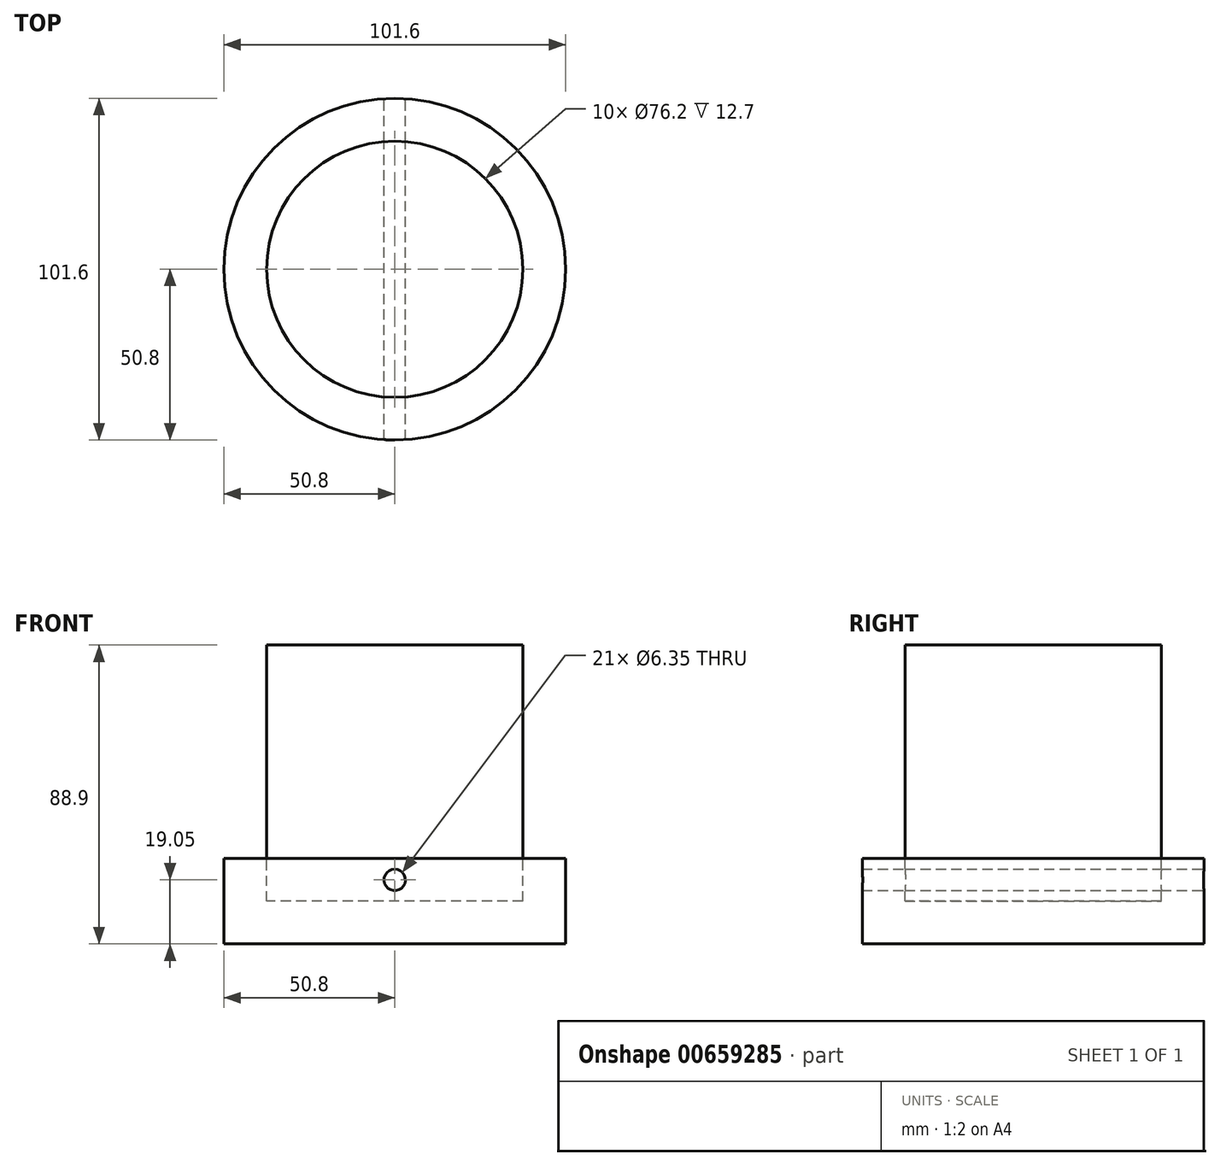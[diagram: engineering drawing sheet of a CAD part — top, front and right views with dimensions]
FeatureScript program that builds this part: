
annotation { "Feature Type Name" : "Feature", "Feature Type Description" : "" }
export const myFeature = defineFeature(function(context is Context, id is Id, definition is map)
    precondition{}
    {
        {
            var Q0;
            Q0=qCreatedBy(makeId("Top.planeOp"),FACE);
            var sketch = newSketch(context, id + "F0", { "sketchPlane" : qUnion([Q0])});
            skCircle(sketch, "E0", {"center": v(0, 0) * mm, "radius": 50.8 * mm});
            skSolve(sketch);
        }
        {
            var Q0;
            Q0 = qSketchRegion(id + "F0", true);
            extrude(context, id + "F1", {"entities" : qUnion([Q0]), "depth" : 25.4 * mm, "offsetDistance" : 25.4 * mm});
        }
        {
            var Q0;
            Q0=makeQuery(id+"F1.opExtrude","CAP_FACE",FACE,{"disambiguationData":[OSD([sQuery(id+"F0.wireOp",EDGE,"E0")])],"isStart":false});
            var sketch = newSketch(context, id + "F2", { "sketchPlane" : qUnion([Q0])});
            skCircle(sketch, "E1", {"center": v(0, 0) * mm, "radius": 38.1 * mm});
            skSolve(sketch);
        }
        {
            var Q0;
            Q0 = qSketchRegion(id + "F2", true);
            extrude(context, id + "F3", {"entities" : qUnion([Q0]), "operationType" : NewBodyOperationType.REMOVE, "oppositeDirection" : true, "depth" : 12.7 * mm, "offsetDistance" : 25.4 * mm});
        }
        {
            var Q0;
            Q0=qCreatedBy(makeId("Front.planeOp"),FACE);
            var sketch = newSketch(context, id + "F4", { "sketchPlane" : qUnion([Q0])});
            skCircle(sketch, "E2", {"center": v(0, 19.05) * mm, "radius": 3.18 * mm});
            skSolve(sketch);
        }
        {
            var Q0;
            Q0=makeQuery(id+"F3.boolean.opBoolean","COPY",FACE,{"derivedFrom":makeQuery(id+"F3.opExtrude","CAP_FACE",FACE,{"disambiguationData":[OSD([sQuery(id+"F2.wireOp",EDGE,"E1")])],"isStart":false})});
            var sketch = newSketch(context, id + "F5", { "sketchPlane" : qUnion([Q0])});
            skCircle(sketch, "E3", {"center": v(0, 0) * mm, "radius": 38.1 * mm});
            skSolve(sketch);
        }
        {
            var Q0;
            Q0 = qSketchRegion(id + "F5", true);
            extrude(context, id + "F6", {"entities" : qUnion([Q0]), "depth" : 76.2 * mm, "offsetDistance" : 25.4 * mm});
        }
        {
            var Q0;
            Q0 = qSketchRegion(id + "F4", true);
            extrude(context, id + "F7", {"entities" : qUnion([Q0]), "operationType" : NewBodyOperationType.REMOVE, "endBound" : BoundingType.SYMMETRIC, "depth" : 101.6 * mm, "offsetDistance" : 25.4 * mm});
        }
    });
